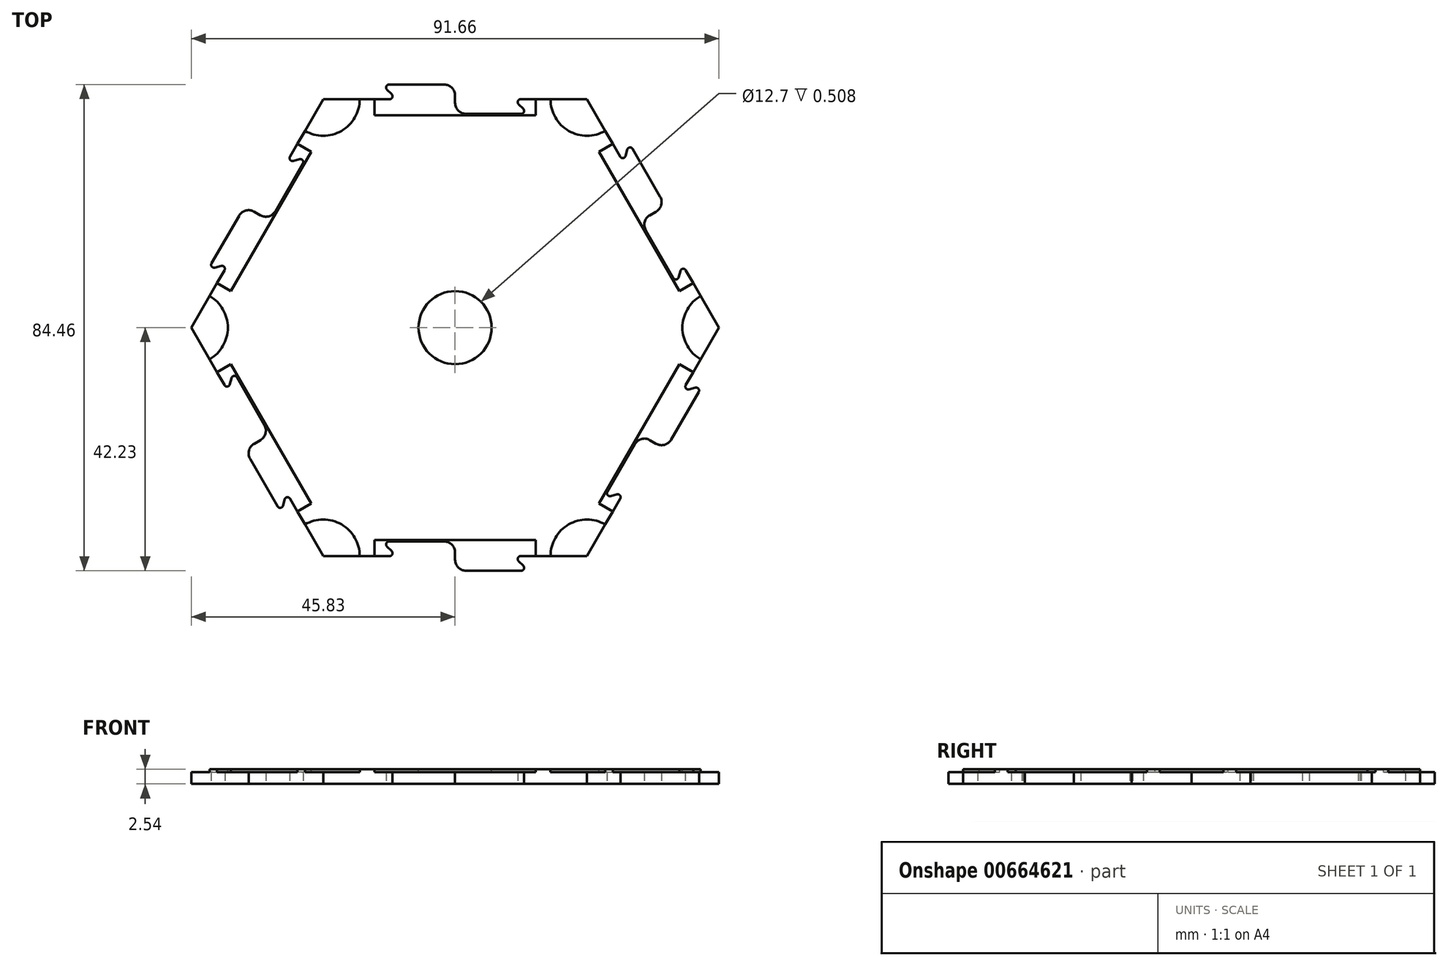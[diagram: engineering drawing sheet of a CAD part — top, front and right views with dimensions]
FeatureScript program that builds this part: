
annotation { "Feature Type Name" : "Feature", "Feature Type Description" : "" }
export const myFeature = defineFeature(function(context is Context, id is Id, definition is map)
    precondition{}
    {
        {
            var Q0;
            Q0=qCreatedBy(makeId("Top.planeOp"),FACE);
            var sketch = newSketch(context, id + "F0", { "sketchPlane" : qUnion([Q0])});
            skCircle(sketch, "E0.cCircle", {"center": v(0, -26.46) * mm, "radius": 13.23 * mm, "construction": true});
            skLineSegment(sketch, "E0.0", {"start": v(22.91, -39.69) * mm, "end": v(-22.91, -39.69) * mm});
            skLineSegment(sketch, "E0.1", {"start": v(-22.91, -39.69) * mm, "end": v(0, 0) * mm});
            skLineSegment(sketch, "E0.2", {"start": v(0, 0) * mm, "end": v(22.91, -39.69) * mm});
            skPoint(sketch, "E0.0.midPoint", {"position": v(0, -39.69) * mm});
            skLineSegment(sketch, "E1", {"start": v(0, -39.69) * mm, "end": v(0, -40.32) * mm});
            skLineSegment(sketch, "E2", {"start": v(1.9, -42.23) * mm, "end": v(11.47, -42.23) * mm});
            skLineSegment(sketch, "E3", {"start": v(11.83, -41.36) * mm, "end": v(11.03, -40.55) * mm});
            skPoint(sketch, "E4.visualSharp", {"position": v(0, -42.23) * mm});
            skPoint(sketch, "E5.visualSharp", {"position": v(12.7, -42.23) * mm});
            skArc(sketch, "E5.filletArc", {"start": v(11.47, -42.23) * mm, "mid": v(11.94, -41.91) * mm, "end": v(11.83, -41.36) * mm});
            skLineSegment(sketch, "E6", {"start": v(11.39, -39.69) * mm, "end": v(22.91, -39.69) * mm});
            skArc(sketch, "E7.filletArc", {"start": v(11.39, -39.69) * mm, "mid": v(10.92, -40) * mm, "end": v(11.03, -40.55) * mm});
            skArc(sketch, "E8.filletArc", {"start": v(0, -40.32) * mm, "mid": v(0.56, -41.67) * mm, "end": v(1.9, -42.23) * mm});
            skLineSegment(sketch, "E9.1.0", {"start": v(-1.9, -37.15) * mm, "end": v(-11.47, -37.15) * mm});
            skArc(sketch, "E9.1.1", {"start": v(0, -39.05) * mm, "mid": v(-0.56, -37.7) * mm, "end": v(-1.9, -37.15) * mm});
            skLineSegment(sketch, "E9.1.2", {"start": v(0, -39.69) * mm, "end": v(0, -39.05) * mm});
            skLineSegment(sketch, "E9.1.3", {"start": v(-11.83, -38.01) * mm, "end": v(-11.03, -38.82) * mm});
            skArc(sketch, "E9.1.4", {"start": v(-11.39, -39.69) * mm, "mid": v(-10.92, -39.37) * mm, "end": v(-11.03, -38.82) * mm});
            skArc(sketch, "E9.1.5", {"start": v(-11.47, -37.15) * mm, "mid": v(-11.94, -37.46) * mm, "end": v(-11.83, -38.01) * mm});
            skSolve(sketch);
        }
        {
            var Q0;
            {var subQ0=sQuery(id+"F0.wireOp",EDGE,"E0.1");Q0=makeQuery(id+"F0.imprint","IMPRINT",FACE,{"disambiguationData":[TD([[makeQuery(id+"F0.imprint","IMPRINT",EDGE,{"derivedFrom":subQ0}),-1.0]])]});}
            var Q1;
            {var subQ0=sQuery(id+"F0.wireOp",EDGE,"97a6bddb-cc4e-44b6-bba3-12cff80ae4aa2.MirrorCS");Q1=makeQuery(id+"F0.imprint","IMPRINT",FACE,{"disambiguationData":[TD([[makeQuery(id+"F0.imprint","IMPRINT",EDGE,{"derivedFrom":subQ0}),-1.0]])]});}
            var Q2;
            {var subQ0=sQuery(id+"F0.wireOp",EDGE,"97a6bddb-cc4e-44b6-bba3-12cff80ae4aa1.MirrorCS");Q2=makeQuery(id+"F0.imprint","IMPRINT",FACE,{"disambiguationData":[TD([[makeQuery(id+"F0.imprint","IMPRINT",EDGE,{"derivedFrom":subQ0}),-1.0]])]});}
            var Q3;
            {var subQ0=sQuery(id+"F0.wireOp",EDGE,"97a6bddb-cc4e-44b6-bba3-12cff80ae4aa0.MirrorCS");Q3=makeQuery(id+"F0.imprint","IMPRINT",FACE,{"disambiguationData":[TD([[makeQuery(id+"F0.imprint","IMPRINT",EDGE,{"derivedFrom":subQ0}),-1.0]])]});}
            var Q4;
            {var subQ0=sQuery(id+"F0.wireOp",EDGE,"bf1687b6-3201-489e-a830-a7b10a865e700.MirrorCS");Q4=makeQuery(id+"F0.imprint","IMPRINT",FACE,{"disambiguationData":[TD([[makeQuery(id+"F0.imprint","IMPRINT",EDGE,{"derivedFrom":subQ0}),-1.0]])]});}
            var Q5;
            {var subQ0=sQuery(id+"F0.wireOp",EDGE,"e4fa4f41-507d-49eb-8017-fd13d7fb7afb0.MirrorCS");Q5=makeQuery(id+"F0.imprint","IMPRINT",FACE,{"disambiguationData":[TD([[makeQuery(id+"F0.imprint","IMPRINT",EDGE,{"derivedFrom":subQ0}),-1.0]])]});}
            var Q6;
            {var subQ0=sQuery(id+"F0.wireOp",EDGE,"ce523281-1682-42e5-b175-8e6fab38ec800.MirrorCS");Q6=makeQuery(id+"F0.imprint","IMPRINT",FACE,{"disambiguationData":[TD([[makeQuery(id+"F0.imprint","IMPRINT",EDGE,{"derivedFrom":subQ0}),-1.0]])]});}
            var Q7;
            {var subQ0=sQuery(id+"F0.wireOp",EDGE,"d5b8cde3-618e-44ad-8592-c6a08a5388a20.MirrorCS");Q7=makeQuery(id+"F0.imprint","IMPRINT",FACE,{"disambiguationData":[TD([[makeQuery(id+"F0.imprint","IMPRINT",EDGE,{"derivedFrom":subQ0}),-1.0]])]});}
            var Q8;
            {var subQ0=sQuery(id+"F0.wireOp",EDGE,"a88186e3-5a36-4d69-b793-0797718b3cf90.MirrorCS");Q8=makeQuery(id+"F0.imprint","IMPRINT",FACE,{"disambiguationData":[TD([[makeQuery(id+"F0.imprint","IMPRINT",EDGE,{"derivedFrom":subQ0}),-1.0]])]});}
            var Q9;
            {var subQ0=sQuery(id+"F0.wireOp",EDGE,"b8ba4a25-16ed-4d6a-869f-626e8081a0210.MirrorCS");Q9=makeQuery(id+"F0.imprint","IMPRINT",FACE,{"disambiguationData":[TD([[makeQuery(id+"F0.imprint","IMPRINT",EDGE,{"derivedFrom":subQ0}),-1.0]])]});}
            var Q10;
            {var subQ0=sQuery(id+"F0.wireOp",EDGE,"5b914c75-573c-406b-9c57-d630d5a647c60.MirrorCS");Q10=makeQuery(id+"F0.imprint","IMPRINT",FACE,{"disambiguationData":[TD([[makeQuery(id+"F0.imprint","IMPRINT",EDGE,{"derivedFrom":subQ0}),-1.0]])]});}
            var Q11;
            {var subQ0=sQuery(id+"F0.wireOp",EDGE,"7752e346-6ae3-4903-9fef-7c2ba14c38f10.MirrorCS");Q11=makeQuery(id+"F0.imprint","IMPRINT",FACE,{"disambiguationData":[TD([[makeQuery(id+"F0.imprint","IMPRINT",EDGE,{"derivedFrom":subQ0}),-1.0]])]});}
            var Q12;
            {var subQ0=sQuery(id+"F0.wireOp",EDGE,"67ecb135-220a-48f5-8a20-4e4477ede5310.MirrorCS");Q12=makeQuery(id+"F0.imprint","IMPRINT",FACE,{"disambiguationData":[TD([[makeQuery(id+"F0.imprint","IMPRINT",EDGE,{"derivedFrom":subQ0}),-1.0]])]});}
            var Q13;
            {var subQ0=sQuery(id+"F0.wireOp",EDGE,"chmzN1dF-lVPi-ufDX-51Gh-vAFPaPJtTRV7");Q13=makeQuery(id+"F0.imprint","IMPRINT",FACE,{"disambiguationData":[TD([[makeQuery(id+"F0.imprint","IMPRINT",EDGE,{"derivedFrom":subQ0}),-1.0]])]});}
            var Q14;
            {var subQ0=sQuery(id+"F0.wireOp",EDGE,"xmj2q76Y-8T0x-Uy3E-bdky-wkXMybDKTkoC");Q14=makeQuery(id+"F0.imprint","IMPRINT",FACE,{"disambiguationData":[TD([[makeQuery(id+"F0.imprint","IMPRINT",EDGE,{"derivedFrom":subQ0}),-1.0]])]});}
            var Q15;
            {var subQ0=sQuery(id+"F0.wireOp",EDGE,"hptf5S9C-4OT9-Tymd-WndI-nW2AmtLXeZ2Y");Q15=makeQuery(id+"F0.imprint","IMPRINT",FACE,{"disambiguationData":[TD([[makeQuery(id+"F0.imprint","IMPRINT",EDGE,{"derivedFrom":subQ0}),-1.0]])]});}
            var Q16;
            {var subQ0=sQuery(id+"F0.wireOp",EDGE,"E1");Q16=makeQuery(id+"F0.imprint","IMPRINT",FACE,{"disambiguationData":[TD([[makeQuery(id+"F0.imprint","IMPRINT",EDGE,{"derivedFrom":subQ0}),1.0]])]});}
            extrude(context, id + "F1", {"entities" : qUnion([Q0, Q1, Q2, Q3, Q4, Q5, Q6, Q7, Q8, Q9, Q10, Q11, Q12, Q13, Q14, Q15, Q16]), "depth" : 2.54 * mm, "offsetDistance" : 25.4 * mm});
        }
        {
            var Q0;
            Q0=makeQuery(id+"F1.opExtrude","SWEPT_BODY",BODY,{"disambiguationData":[OSD([sQuery(id+"F0.wireOp",EDGE,"E0.0"),sQuery(id+"F0.wireOp",EDGE,"E0.1"),sQuery(id+"F0.wireOp",EDGE,"E0.2"),sQuery(id+"F0.wireOp",EDGE,"Ihc1fdpb-C9ge-KW9p-kyAT-bs0RLZlIlIaE"),sQuery(id+"F0.wireOp",EDGE,"87ea3ed5-fdca-4bcd-8325-5824a1b2b9b6.1.0.0"),sQuery(id+"F0.wireOp",EDGE,"87ea3ed5-fdca-4bcd-8325-5824a1b2b9b6.2.0.0"),sQuery(id+"F0.wireOp",EDGE,"87ea3ed5-fdca-4bcd-8325-5824a1b2b9b6.3.0.0"),sQuery(id+"F0.wireOp",EDGE,"be1f27a8-b5cd-4a3d-9b83-b1ceea2719dc.1.0.0"),sQuery(id+"F0.wireOp",EDGE,"be1f27a8-b5cd-4a3d-9b83-b1ceea2719dc.2.0.0"),sQuery(id+"F0.wireOp",EDGE,"be1f27a8-b5cd-4a3d-9b83-b1ceea2719dc.3.0.0"),sQuery(id+"F0.wireOp",EDGE,"be1f27a8-b5cd-4a3d-9b83-b1ceea2719dc.4.0.0"),sQuery(id+"F0.wireOp",EDGE,"97a6bddb-cc4e-44b6-bba3-12cff80ae4aa0.MirrorCS"),sQuery(id+"F0.wireOp",EDGE,"97a6bddb-cc4e-44b6-bba3-12cff80ae4aa1.MirrorCS"),sQuery(id+"F0.wireOp",EDGE,"97a6bddb-cc4e-44b6-bba3-12cff80ae4aa2.MirrorCS"),sQuery(id+"F0.wireOp",EDGE,"bf1687b6-3201-489e-a830-a7b10a865e700.MirrorCS"),sQuery(id+"F0.wireOp",EDGE,"e4fa4f41-507d-49eb-8017-fd13d7fb7afb0.MirrorCS"),sQuery(id+"F0.wireOp",EDGE,"ce523281-1682-42e5-b175-8e6fab38ec800.MirrorCS"),sQuery(id+"F0.wireOp",EDGE,"d5b8cde3-618e-44ad-8592-c6a08a5388a20.MirrorCS"),sQuery(id+"F0.wireOp",EDGE,"a88186e3-5a36-4d69-b793-0797718b3cf90.MirrorCS")])]});
            var Q1;
            Q1=makeQuery(id+"F1.opExtrude","SWEPT_EDGE",EDGE,{"disambiguationData":[OSD([sQuery(id+"F0.wireOp",EDGE,"E0.1"),sQuery(id+"F0.wireOp",EDGE,"E0.2")])]});
            circularPattern(context, id + "F2", {"entities" : qUnion([Q0]), "axis" : qUnion([Q1]), "angle" : 360 * degree, "instanceCount" : 6, "equalSpace" : true});
        }
        {
            var Q0;
            Q0=makeQuery(id+"F1.opExtrude","SWEPT_BODY",BODY,{"disambiguationData":[OSD([sQuery(id+"F0.wireOp",EDGE,"E0.0"),sQuery(id+"F0.wireOp",EDGE,"E0.1"),sQuery(id+"F0.wireOp",EDGE,"E0.2"),sQuery(id+"F0.wireOp",EDGE,"Ihc1fdpb-C9ge-KW9p-kyAT-bs0RLZlIlIaE"),sQuery(id+"F0.wireOp",EDGE,"87ea3ed5-fdca-4bcd-8325-5824a1b2b9b6.1.0.0"),sQuery(id+"F0.wireOp",EDGE,"87ea3ed5-fdca-4bcd-8325-5824a1b2b9b6.2.0.0"),sQuery(id+"F0.wireOp",EDGE,"87ea3ed5-fdca-4bcd-8325-5824a1b2b9b6.3.0.0"),sQuery(id+"F0.wireOp",EDGE,"be1f27a8-b5cd-4a3d-9b83-b1ceea2719dc.1.0.0"),sQuery(id+"F0.wireOp",EDGE,"be1f27a8-b5cd-4a3d-9b83-b1ceea2719dc.2.0.0"),sQuery(id+"F0.wireOp",EDGE,"be1f27a8-b5cd-4a3d-9b83-b1ceea2719dc.3.0.0"),sQuery(id+"F0.wireOp",EDGE,"be1f27a8-b5cd-4a3d-9b83-b1ceea2719dc.4.0.0"),sQuery(id+"F0.wireOp",EDGE,"97a6bddb-cc4e-44b6-bba3-12cff80ae4aa0.MirrorCS"),sQuery(id+"F0.wireOp",EDGE,"97a6bddb-cc4e-44b6-bba3-12cff80ae4aa1.MirrorCS"),sQuery(id+"F0.wireOp",EDGE,"97a6bddb-cc4e-44b6-bba3-12cff80ae4aa2.MirrorCS"),sQuery(id+"F0.wireOp",EDGE,"bf1687b6-3201-489e-a830-a7b10a865e700.MirrorCS"),sQuery(id+"F0.wireOp",EDGE,"e4fa4f41-507d-49eb-8017-fd13d7fb7afb0.MirrorCS"),sQuery(id+"F0.wireOp",EDGE,"ce523281-1682-42e5-b175-8e6fab38ec800.MirrorCS"),sQuery(id+"F0.wireOp",EDGE,"d5b8cde3-618e-44ad-8592-c6a08a5388a20.MirrorCS"),sQuery(id+"F0.wireOp",EDGE,"a88186e3-5a36-4d69-b793-0797718b3cf90.MirrorCS")])]});
            var Q1;
            Q1=makeQuery(id+"F2.opPattern","COPY",BODY,{"derivedFrom":makeQuery(id+"F1.opExtrude","SWEPT_BODY",BODY,{"disambiguationData":[OSD([sQuery(id+"F0.wireOp",EDGE,"E0.0"),sQuery(id+"F0.wireOp",EDGE,"E0.1"),sQuery(id+"F0.wireOp",EDGE,"E0.2"),sQuery(id+"F0.wireOp",EDGE,"Ihc1fdpb-C9ge-KW9p-kyAT-bs0RLZlIlIaE"),sQuery(id+"F0.wireOp",EDGE,"87ea3ed5-fdca-4bcd-8325-5824a1b2b9b6.1.0.0"),sQuery(id+"F0.wireOp",EDGE,"87ea3ed5-fdca-4bcd-8325-5824a1b2b9b6.2.0.0"),sQuery(id+"F0.wireOp",EDGE,"87ea3ed5-fdca-4bcd-8325-5824a1b2b9b6.3.0.0"),sQuery(id+"F0.wireOp",EDGE,"be1f27a8-b5cd-4a3d-9b83-b1ceea2719dc.1.0.0"),sQuery(id+"F0.wireOp",EDGE,"be1f27a8-b5cd-4a3d-9b83-b1ceea2719dc.2.0.0"),sQuery(id+"F0.wireOp",EDGE,"be1f27a8-b5cd-4a3d-9b83-b1ceea2719dc.3.0.0"),sQuery(id+"F0.wireOp",EDGE,"be1f27a8-b5cd-4a3d-9b83-b1ceea2719dc.4.0.0"),sQuery(id+"F0.wireOp",EDGE,"97a6bddb-cc4e-44b6-bba3-12cff80ae4aa0.MirrorCS"),sQuery(id+"F0.wireOp",EDGE,"97a6bddb-cc4e-44b6-bba3-12cff80ae4aa1.MirrorCS"),sQuery(id+"F0.wireOp",EDGE,"97a6bddb-cc4e-44b6-bba3-12cff80ae4aa2.MirrorCS"),sQuery(id+"F0.wireOp",EDGE,"bf1687b6-3201-489e-a830-a7b10a865e700.MirrorCS"),sQuery(id+"F0.wireOp",EDGE,"e4fa4f41-507d-49eb-8017-fd13d7fb7afb0.MirrorCS"),sQuery(id+"F0.wireOp",EDGE,"ce523281-1682-42e5-b175-8e6fab38ec800.MirrorCS"),sQuery(id+"F0.wireOp",EDGE,"d5b8cde3-618e-44ad-8592-c6a08a5388a20.MirrorCS"),sQuery(id+"F0.wireOp",EDGE,"a88186e3-5a36-4d69-b793-0797718b3cf90.MirrorCS")])]}),"instanceName":"1"});
            var Q2;
            Q2=makeQuery(id+"F2.opPattern","COPY",BODY,{"derivedFrom":makeQuery(id+"F1.opExtrude","SWEPT_BODY",BODY,{"disambiguationData":[OSD([sQuery(id+"F0.wireOp",EDGE,"E0.0"),sQuery(id+"F0.wireOp",EDGE,"E0.1"),sQuery(id+"F0.wireOp",EDGE,"E0.2"),sQuery(id+"F0.wireOp",EDGE,"Ihc1fdpb-C9ge-KW9p-kyAT-bs0RLZlIlIaE"),sQuery(id+"F0.wireOp",EDGE,"87ea3ed5-fdca-4bcd-8325-5824a1b2b9b6.1.0.0"),sQuery(id+"F0.wireOp",EDGE,"87ea3ed5-fdca-4bcd-8325-5824a1b2b9b6.2.0.0"),sQuery(id+"F0.wireOp",EDGE,"87ea3ed5-fdca-4bcd-8325-5824a1b2b9b6.3.0.0"),sQuery(id+"F0.wireOp",EDGE,"be1f27a8-b5cd-4a3d-9b83-b1ceea2719dc.1.0.0"),sQuery(id+"F0.wireOp",EDGE,"be1f27a8-b5cd-4a3d-9b83-b1ceea2719dc.2.0.0"),sQuery(id+"F0.wireOp",EDGE,"be1f27a8-b5cd-4a3d-9b83-b1ceea2719dc.3.0.0"),sQuery(id+"F0.wireOp",EDGE,"be1f27a8-b5cd-4a3d-9b83-b1ceea2719dc.4.0.0"),sQuery(id+"F0.wireOp",EDGE,"97a6bddb-cc4e-44b6-bba3-12cff80ae4aa0.MirrorCS"),sQuery(id+"F0.wireOp",EDGE,"97a6bddb-cc4e-44b6-bba3-12cff80ae4aa1.MirrorCS"),sQuery(id+"F0.wireOp",EDGE,"97a6bddb-cc4e-44b6-bba3-12cff80ae4aa2.MirrorCS"),sQuery(id+"F0.wireOp",EDGE,"bf1687b6-3201-489e-a830-a7b10a865e700.MirrorCS"),sQuery(id+"F0.wireOp",EDGE,"e4fa4f41-507d-49eb-8017-fd13d7fb7afb0.MirrorCS"),sQuery(id+"F0.wireOp",EDGE,"ce523281-1682-42e5-b175-8e6fab38ec800.MirrorCS"),sQuery(id+"F0.wireOp",EDGE,"d5b8cde3-618e-44ad-8592-c6a08a5388a20.MirrorCS"),sQuery(id+"F0.wireOp",EDGE,"a88186e3-5a36-4d69-b793-0797718b3cf90.MirrorCS")])]}),"instanceName":"2"});
            var Q3;
            Q3=makeQuery(id+"F2.opPattern","COPY",BODY,{"derivedFrom":makeQuery(id+"F1.opExtrude","SWEPT_BODY",BODY,{"disambiguationData":[OSD([sQuery(id+"F0.wireOp",EDGE,"E0.0"),sQuery(id+"F0.wireOp",EDGE,"E0.1"),sQuery(id+"F0.wireOp",EDGE,"E0.2"),sQuery(id+"F0.wireOp",EDGE,"Ihc1fdpb-C9ge-KW9p-kyAT-bs0RLZlIlIaE"),sQuery(id+"F0.wireOp",EDGE,"87ea3ed5-fdca-4bcd-8325-5824a1b2b9b6.1.0.0"),sQuery(id+"F0.wireOp",EDGE,"87ea3ed5-fdca-4bcd-8325-5824a1b2b9b6.2.0.0"),sQuery(id+"F0.wireOp",EDGE,"87ea3ed5-fdca-4bcd-8325-5824a1b2b9b6.3.0.0"),sQuery(id+"F0.wireOp",EDGE,"be1f27a8-b5cd-4a3d-9b83-b1ceea2719dc.1.0.0"),sQuery(id+"F0.wireOp",EDGE,"be1f27a8-b5cd-4a3d-9b83-b1ceea2719dc.2.0.0"),sQuery(id+"F0.wireOp",EDGE,"be1f27a8-b5cd-4a3d-9b83-b1ceea2719dc.3.0.0"),sQuery(id+"F0.wireOp",EDGE,"be1f27a8-b5cd-4a3d-9b83-b1ceea2719dc.4.0.0"),sQuery(id+"F0.wireOp",EDGE,"97a6bddb-cc4e-44b6-bba3-12cff80ae4aa0.MirrorCS"),sQuery(id+"F0.wireOp",EDGE,"97a6bddb-cc4e-44b6-bba3-12cff80ae4aa1.MirrorCS"),sQuery(id+"F0.wireOp",EDGE,"97a6bddb-cc4e-44b6-bba3-12cff80ae4aa2.MirrorCS"),sQuery(id+"F0.wireOp",EDGE,"bf1687b6-3201-489e-a830-a7b10a865e700.MirrorCS"),sQuery(id+"F0.wireOp",EDGE,"e4fa4f41-507d-49eb-8017-fd13d7fb7afb0.MirrorCS"),sQuery(id+"F0.wireOp",EDGE,"ce523281-1682-42e5-b175-8e6fab38ec800.MirrorCS"),sQuery(id+"F0.wireOp",EDGE,"d5b8cde3-618e-44ad-8592-c6a08a5388a20.MirrorCS"),sQuery(id+"F0.wireOp",EDGE,"a88186e3-5a36-4d69-b793-0797718b3cf90.MirrorCS")])]}),"instanceName":"3"});
            var Q4;
            Q4=makeQuery(id+"F2.opPattern","COPY",BODY,{"derivedFrom":makeQuery(id+"F1.opExtrude","SWEPT_BODY",BODY,{"disambiguationData":[OSD([sQuery(id+"F0.wireOp",EDGE,"E0.0"),sQuery(id+"F0.wireOp",EDGE,"E0.1"),sQuery(id+"F0.wireOp",EDGE,"E0.2"),sQuery(id+"F0.wireOp",EDGE,"Ihc1fdpb-C9ge-KW9p-kyAT-bs0RLZlIlIaE"),sQuery(id+"F0.wireOp",EDGE,"87ea3ed5-fdca-4bcd-8325-5824a1b2b9b6.1.0.0"),sQuery(id+"F0.wireOp",EDGE,"87ea3ed5-fdca-4bcd-8325-5824a1b2b9b6.2.0.0"),sQuery(id+"F0.wireOp",EDGE,"87ea3ed5-fdca-4bcd-8325-5824a1b2b9b6.3.0.0"),sQuery(id+"F0.wireOp",EDGE,"be1f27a8-b5cd-4a3d-9b83-b1ceea2719dc.1.0.0"),sQuery(id+"F0.wireOp",EDGE,"be1f27a8-b5cd-4a3d-9b83-b1ceea2719dc.2.0.0"),sQuery(id+"F0.wireOp",EDGE,"be1f27a8-b5cd-4a3d-9b83-b1ceea2719dc.3.0.0"),sQuery(id+"F0.wireOp",EDGE,"be1f27a8-b5cd-4a3d-9b83-b1ceea2719dc.4.0.0"),sQuery(id+"F0.wireOp",EDGE,"97a6bddb-cc4e-44b6-bba3-12cff80ae4aa0.MirrorCS"),sQuery(id+"F0.wireOp",EDGE,"97a6bddb-cc4e-44b6-bba3-12cff80ae4aa1.MirrorCS"),sQuery(id+"F0.wireOp",EDGE,"97a6bddb-cc4e-44b6-bba3-12cff80ae4aa2.MirrorCS"),sQuery(id+"F0.wireOp",EDGE,"bf1687b6-3201-489e-a830-a7b10a865e700.MirrorCS"),sQuery(id+"F0.wireOp",EDGE,"e4fa4f41-507d-49eb-8017-fd13d7fb7afb0.MirrorCS"),sQuery(id+"F0.wireOp",EDGE,"ce523281-1682-42e5-b175-8e6fab38ec800.MirrorCS"),sQuery(id+"F0.wireOp",EDGE,"d5b8cde3-618e-44ad-8592-c6a08a5388a20.MirrorCS"),sQuery(id+"F0.wireOp",EDGE,"a88186e3-5a36-4d69-b793-0797718b3cf90.MirrorCS")])]}),"instanceName":"4"});
            var Q5;
            Q5=makeQuery(id+"F2.opPattern","COPY",BODY,{"derivedFrom":makeQuery(id+"F1.opExtrude","SWEPT_BODY",BODY,{"disambiguationData":[OSD([sQuery(id+"F0.wireOp",EDGE,"E0.0"),sQuery(id+"F0.wireOp",EDGE,"E0.1"),sQuery(id+"F0.wireOp",EDGE,"E0.2"),sQuery(id+"F0.wireOp",EDGE,"Ihc1fdpb-C9ge-KW9p-kyAT-bs0RLZlIlIaE"),sQuery(id+"F0.wireOp",EDGE,"87ea3ed5-fdca-4bcd-8325-5824a1b2b9b6.1.0.0"),sQuery(id+"F0.wireOp",EDGE,"87ea3ed5-fdca-4bcd-8325-5824a1b2b9b6.2.0.0"),sQuery(id+"F0.wireOp",EDGE,"87ea3ed5-fdca-4bcd-8325-5824a1b2b9b6.3.0.0"),sQuery(id+"F0.wireOp",EDGE,"be1f27a8-b5cd-4a3d-9b83-b1ceea2719dc.1.0.0"),sQuery(id+"F0.wireOp",EDGE,"be1f27a8-b5cd-4a3d-9b83-b1ceea2719dc.2.0.0"),sQuery(id+"F0.wireOp",EDGE,"be1f27a8-b5cd-4a3d-9b83-b1ceea2719dc.3.0.0"),sQuery(id+"F0.wireOp",EDGE,"be1f27a8-b5cd-4a3d-9b83-b1ceea2719dc.4.0.0"),sQuery(id+"F0.wireOp",EDGE,"97a6bddb-cc4e-44b6-bba3-12cff80ae4aa0.MirrorCS"),sQuery(id+"F0.wireOp",EDGE,"97a6bddb-cc4e-44b6-bba3-12cff80ae4aa1.MirrorCS"),sQuery(id+"F0.wireOp",EDGE,"97a6bddb-cc4e-44b6-bba3-12cff80ae4aa2.MirrorCS"),sQuery(id+"F0.wireOp",EDGE,"bf1687b6-3201-489e-a830-a7b10a865e700.MirrorCS"),sQuery(id+"F0.wireOp",EDGE,"e4fa4f41-507d-49eb-8017-fd13d7fb7afb0.MirrorCS"),sQuery(id+"F0.wireOp",EDGE,"ce523281-1682-42e5-b175-8e6fab38ec800.MirrorCS"),sQuery(id+"F0.wireOp",EDGE,"d5b8cde3-618e-44ad-8592-c6a08a5388a20.MirrorCS"),sQuery(id+"F0.wireOp",EDGE,"a88186e3-5a36-4d69-b793-0797718b3cf90.MirrorCS")])]}),"instanceName":"5"});
            booleanBodies(context, id + "F3", {"operationType" : BooleanOperationType.UNION, "tools" : qUnion([Q0, Q1, Q2, Q3, Q4, Q5])});
        }
        {
            var Q0;
            {var subQ0=makeQuery(id+"F1.opExtrude","CAP_FACE",FACE,{"disambiguationData":[OSD([sQuery(id+"F0.wireOp",EDGE,"E0.0"),sQuery(id+"F0.wireOp",EDGE,"E0.1"),sQuery(id+"F0.wireOp",EDGE,"E0.2"),sQuery(id+"F0.wireOp",EDGE,"E1"),sQuery(id+"F0.wireOp",EDGE,"E2"),sQuery(id+"F0.wireOp",EDGE,"E3"),sQuery(id+"F0.wireOp",EDGE,"E5.filletArc"),sQuery(id+"F0.wireOp",EDGE,"E6"),sQuery(id+"F0.wireOp",EDGE,"E7.filletArc"),sQuery(id+"F0.wireOp",EDGE,"E8.filletArc"),sQuery(id+"F0.wireOp",EDGE,"E9.1.0"),sQuery(id+"F0.wireOp",EDGE,"E9.1.1"),sQuery(id+"F0.wireOp",EDGE,"E9.1.2"),sQuery(id+"F0.wireOp",EDGE,"E9.1.3"),sQuery(id+"F0.wireOp",EDGE,"E9.1.4"),sQuery(id+"F0.wireOp",EDGE,"E9.1.5")])],"isStart":false});Q0=makeQuery(id+"F3.opBoolean","MERGE",FACE,{"derivedFrom":[subQ0,makeQuery(id+"F2.opPattern","COPY",FACE,{"derivedFrom":subQ0,"instanceName":"1"}),makeQuery(id+"F2.opPattern","COPY",FACE,{"derivedFrom":subQ0,"instanceName":"2"}),makeQuery(id+"F2.opPattern","COPY",FACE,{"derivedFrom":subQ0,"instanceName":"3"}),makeQuery(id+"F2.opPattern","COPY",FACE,{"derivedFrom":subQ0,"instanceName":"4"}),makeQuery(id+"F2.opPattern","COPY",FACE,{"derivedFrom":subQ0,"instanceName":"5"})]});}
            var sketch = newSketch(context, id + "F4", { "sketchPlane" : qUnion([Q0])});
            skLineSegment(sketch, "E10.bottom", {"start": v(-13.97, -36.9) * mm, "end": v(13.97, -36.9) * mm});
            skLineSegment(sketch, "E10.top", {"start": v(-13.97, -42.48) * mm, "end": v(13.97, -42.48) * mm});
            skLineSegment(sketch, "E10.left", {"start": v(-13.97, -36.9) * mm, "end": v(-13.97, -42.48) * mm});
            skLineSegment(sketch, "E10.right", {"start": v(13.97, -36.9) * mm, "end": v(13.97, -42.48) * mm});
            skCircle(sketch, "E11", {"center": v(0, 0) * mm, "radius": 6.35 * mm});
            skLineSegment(sketch, "E12.1.0", {"start": v(29.8, -33.34) * mm, "end": v(43.78, -9.14) * mm});
            skLineSegment(sketch, "E12.1.1", {"start": v(24.97, -30.55) * mm, "end": v(29.8, -33.34) * mm});
            skLineSegment(sketch, "E12.1.2", {"start": v(24.97, -30.55) * mm, "end": v(38.94, -6.35) * mm});
            skLineSegment(sketch, "E12.1.3", {"start": v(38.94, -6.35) * mm, "end": v(43.78, -9.14) * mm});
            skLineSegment(sketch, "E12.2.0", {"start": v(43.78, 9.14) * mm, "end": v(29.8, 33.34) * mm});
            skLineSegment(sketch, "E12.2.1", {"start": v(38.94, 6.35) * mm, "end": v(43.78, 9.14) * mm});
            skLineSegment(sketch, "E12.2.2", {"start": v(38.94, 6.35) * mm, "end": v(24.97, 30.55) * mm});
            skLineSegment(sketch, "E12.2.3", {"start": v(24.97, 30.55) * mm, "end": v(29.8, 33.34) * mm});
            skLineSegment(sketch, "E12.3.0", {"start": v(13.97, 42.48) * mm, "end": v(-13.97, 42.48) * mm});
            skLineSegment(sketch, "E12.3.1", {"start": v(13.97, 36.9) * mm, "end": v(13.97, 42.48) * mm});
            skLineSegment(sketch, "E12.3.2", {"start": v(13.97, 36.9) * mm, "end": v(-13.97, 36.9) * mm});
            skLineSegment(sketch, "E12.3.3", {"start": v(-13.97, 36.9) * mm, "end": v(-13.97, 42.48) * mm});
            skLineSegment(sketch, "E12.4.0", {"start": v(-29.8, 33.34) * mm, "end": v(-43.78, 9.14) * mm});
            skLineSegment(sketch, "E12.4.1", {"start": v(-24.97, 30.55) * mm, "end": v(-29.8, 33.34) * mm});
            skLineSegment(sketch, "E12.4.2", {"start": v(-24.97, 30.55) * mm, "end": v(-38.94, 6.35) * mm});
            skLineSegment(sketch, "E12.4.3", {"start": v(-38.94, 6.35) * mm, "end": v(-43.78, 9.14) * mm});
            skLineSegment(sketch, "E12.5.0", {"start": v(-43.78, -9.14) * mm, "end": v(-29.8, -33.34) * mm});
            skLineSegment(sketch, "E12.5.1", {"start": v(-38.94, -6.35) * mm, "end": v(-43.78, -9.14) * mm});
            skLineSegment(sketch, "E12.5.2", {"start": v(-38.94, -6.35) * mm, "end": v(-24.97, -30.55) * mm});
            skLineSegment(sketch, "E12.5.3", {"start": v(-24.97, -30.55) * mm, "end": v(-29.8, -33.34) * mm});
            skCircle(sketch, "E13", {"center": v(22.91, -39.69) * mm, "radius": 6.35 * mm});
            skCircle(sketch, "E14.1.0", {"center": v(45.83, 0) * mm, "radius": 6.35 * mm});
            skCircle(sketch, "E14.2.0", {"center": v(22.91, 39.69) * mm, "radius": 6.35 * mm});
            skCircle(sketch, "E14.3.0", {"center": v(-22.91, 39.69) * mm, "radius": 6.35 * mm});
            skCircle(sketch, "E14.4.0", {"center": v(-45.83, 0) * mm, "radius": 6.35 * mm});
            skCircle(sketch, "E14.5.0", {"center": v(-22.91, -39.69) * mm, "radius": 6.35 * mm});
            skSolve(sketch);
        }
        {
            var Q0;
            Q0=makeQuery(id+"F4.imprint","IMPRINT",FACE,{"disambiguationData":[TD([[makeQuery(id+"F4.imprint","IMPRINT",EDGE,{"derivedFrom":sQuery(id+"F4.wireOp",EDGE,"E11")}),1.0]])]});
            var Q1;
            Q1=makeQuery(id+"F4.imprint","IMPRINT",FACE,{"disambiguationData":[TD([[makeQuery(id+"F4.imprint","IMPRINT",EDGE,{"derivedFrom":makeQuery(id+"F1.opExtrude","CAP_EDGE",EDGE,{"disambiguationData":[OSD([sQuery(id+"F0.wireOp",EDGE,"E3")])],"isStart":false})}),1.0]])]});
            var Q2;
            Q2=makeQuery(id+"F4.imprint","IMPRINT",FACE,{"disambiguationData":[TD([[makeQuery(id+"F4.imprint","IMPRINT",EDGE,{"derivedFrom":makeQuery(id+"F1.opExtrude","CAP_EDGE",EDGE,{"disambiguationData":[OSD([sQuery(id+"F0.wireOp",EDGE,"E9.1.3")])],"isStart":false})}),-1.0]])]});
            var Q3;
            Q3=makeQuery(id+"F4.imprint","IMPRINT",FACE,{"disambiguationData":[TD([[makeQuery(id+"F4.imprint","IMPRINT",EDGE,{"derivedFrom":makeQuery(id+"F2.opPattern","COPY",EDGE,{"derivedFrom":makeQuery(id+"F1.opExtrude","CAP_EDGE",EDGE,{"disambiguationData":[OSD([sQuery(id+"F0.wireOp",EDGE,"E9.1.3")])],"isStart":false}),"instanceName":"5"})}),-1.0]])]});
            var Q4;
            Q4=makeQuery(id+"F4.imprint","IMPRINT",FACE,{"disambiguationData":[TD([[makeQuery(id+"F4.imprint","IMPRINT",EDGE,{"derivedFrom":makeQuery(id+"F2.opPattern","COPY",EDGE,{"derivedFrom":makeQuery(id+"F1.opExtrude","CAP_EDGE",EDGE,{"disambiguationData":[OSD([sQuery(id+"F0.wireOp",EDGE,"E3")])],"isStart":false}),"instanceName":"5"})}),1.0]])]});
            var Q5;
            Q5=makeQuery(id+"F4.imprint","IMPRINT",FACE,{"disambiguationData":[TD([[makeQuery(id+"F4.imprint","IMPRINT",EDGE,{"derivedFrom":makeQuery(id+"F2.opPattern","COPY",EDGE,{"derivedFrom":makeQuery(id+"F1.opExtrude","CAP_EDGE",EDGE,{"disambiguationData":[OSD([sQuery(id+"F0.wireOp",EDGE,"E9.1.3")])],"isStart":false}),"instanceName":"4"})}),-1.0]])]});
            var Q6;
            Q6=makeQuery(id+"F4.imprint","IMPRINT",FACE,{"disambiguationData":[TD([[makeQuery(id+"F4.imprint","IMPRINT",EDGE,{"derivedFrom":makeQuery(id+"F2.opPattern","COPY",EDGE,{"derivedFrom":makeQuery(id+"F1.opExtrude","CAP_EDGE",EDGE,{"disambiguationData":[OSD([sQuery(id+"F0.wireOp",EDGE,"E3")])],"isStart":false}),"instanceName":"4"})}),1.0]])]});
            var Q7;
            Q7=makeQuery(id+"F4.imprint","IMPRINT",FACE,{"disambiguationData":[TD([[makeQuery(id+"F4.imprint","IMPRINT",EDGE,{"derivedFrom":makeQuery(id+"F2.opPattern","COPY",EDGE,{"derivedFrom":makeQuery(id+"F1.opExtrude","CAP_EDGE",EDGE,{"disambiguationData":[OSD([sQuery(id+"F0.wireOp",EDGE,"E9.1.3")])],"isStart":false}),"instanceName":"3"})}),-1.0]])]});
            var Q8;
            Q8=makeQuery(id+"F4.imprint","IMPRINT",FACE,{"disambiguationData":[TD([[makeQuery(id+"F4.imprint","IMPRINT",EDGE,{"derivedFrom":makeQuery(id+"F2.opPattern","COPY",EDGE,{"derivedFrom":makeQuery(id+"F1.opExtrude","CAP_EDGE",EDGE,{"disambiguationData":[OSD([sQuery(id+"F0.wireOp",EDGE,"E3")])],"isStart":false}),"instanceName":"3"})}),1.0]])]});
            var Q9;
            Q9=makeQuery(id+"F4.imprint","IMPRINT",FACE,{"disambiguationData":[TD([[makeQuery(id+"F4.imprint","IMPRINT",EDGE,{"derivedFrom":makeQuery(id+"F2.opPattern","COPY",EDGE,{"derivedFrom":makeQuery(id+"F1.opExtrude","CAP_EDGE",EDGE,{"disambiguationData":[OSD([sQuery(id+"F0.wireOp",EDGE,"E9.1.3")])],"isStart":false}),"instanceName":"2"})}),-1.0]])]});
            var Q10;
            Q10=makeQuery(id+"F4.imprint","IMPRINT",FACE,{"disambiguationData":[TD([[makeQuery(id+"F4.imprint","IMPRINT",EDGE,{"derivedFrom":makeQuery(id+"F2.opPattern","COPY",EDGE,{"derivedFrom":makeQuery(id+"F1.opExtrude","CAP_EDGE",EDGE,{"disambiguationData":[OSD([sQuery(id+"F0.wireOp",EDGE,"E3")])],"isStart":false}),"instanceName":"2"})}),1.0]])]});
            var Q11;
            Q11=makeQuery(id+"F4.imprint","IMPRINT",FACE,{"disambiguationData":[TD([[makeQuery(id+"F4.imprint","IMPRINT",EDGE,{"derivedFrom":makeQuery(id+"F2.opPattern","COPY",EDGE,{"derivedFrom":makeQuery(id+"F1.opExtrude","CAP_EDGE",EDGE,{"disambiguationData":[OSD([sQuery(id+"F0.wireOp",EDGE,"E9.1.3")])],"isStart":false}),"instanceName":"1"})}),-1.0]])]});
            var Q12;
            Q12=makeQuery(id+"F4.imprint","IMPRINT",FACE,{"disambiguationData":[TD([[makeQuery(id+"F4.imprint","IMPRINT",EDGE,{"derivedFrom":makeQuery(id+"F2.opPattern","COPY",EDGE,{"derivedFrom":makeQuery(id+"F1.opExtrude","CAP_EDGE",EDGE,{"disambiguationData":[OSD([sQuery(id+"F0.wireOp",EDGE,"E3")])],"isStart":false}),"instanceName":"1"})}),1.0]])]});
            var Q13;
            {var subQ0=sQuery(id+"F4.wireOp",EDGE,"E14.5.0");var subQ1=makeQuery(id+"F1.opExtrude","CAP_EDGE",EDGE,{"disambiguationData":[OSD([sQuery(id+"F0.wireOp",EDGE,"E0.0")])],"isStart":false});var subQ2=makeQuery(id+"F4.imprint","INTERSECT",VERTEX,{"derivedFrom":[subQ1,subQ0]});Q13=makeQuery(id+"F4.imprint","IMPRINT",FACE,{"disambiguationData":[TD([[makeQuery(id+"F4.imprint","IMPRINT",EDGE,{"disambiguationData":[TD([[subQ2,-1.0]])],"derivedFrom":subQ0}),1.0]])]});}
            var Q14;
            {var subQ0=sQuery(id+"F4.wireOp",EDGE,"E13");var subQ1=makeQuery(id+"F1.opExtrude","CAP_EDGE",EDGE,{"disambiguationData":[OSD([sQuery(id+"F0.wireOp",EDGE,"E6")])],"isStart":false});var subQ2=makeQuery(id+"F4.imprint","INTERSECT",VERTEX,{"derivedFrom":[subQ1,subQ0]});Q14=makeQuery(id+"F4.imprint","IMPRINT",FACE,{"disambiguationData":[TD([[makeQuery(id+"F4.imprint","IMPRINT",EDGE,{"disambiguationData":[TD([[subQ2,1.0]])],"derivedFrom":subQ0}),1.0]])]});}
            var Q15;
            {var subQ0=sQuery(id+"F4.wireOp",EDGE,"E14.1.0");var subQ1=makeQuery(id+"F2.opPattern","COPY",EDGE,{"derivedFrom":makeQuery(id+"F1.opExtrude","CAP_EDGE",EDGE,{"disambiguationData":[OSD([sQuery(id+"F0.wireOp",EDGE,"E0.0")])],"isStart":false}),"instanceName":"4"});var subQ2=makeQuery(id+"F4.imprint","INTERSECT",VERTEX,{"derivedFrom":[subQ1,subQ0]});Q15=makeQuery(id+"F4.imprint","IMPRINT",FACE,{"disambiguationData":[TD([[makeQuery(id+"F4.imprint","IMPRINT",EDGE,{"disambiguationData":[TD([[subQ2,-1.0]])],"derivedFrom":subQ0}),1.0]])]});}
            var Q16;
            {var subQ0=sQuery(id+"F4.wireOp",EDGE,"E14.2.0");var subQ1=makeQuery(id+"F2.opPattern","COPY",EDGE,{"derivedFrom":makeQuery(id+"F1.opExtrude","CAP_EDGE",EDGE,{"disambiguationData":[OSD([sQuery(id+"F0.wireOp",EDGE,"E0.0")])],"isStart":false}),"instanceName":"3"});var subQ2=makeQuery(id+"F4.imprint","INTERSECT",VERTEX,{"derivedFrom":[subQ1,subQ0]});Q16=makeQuery(id+"F4.imprint","IMPRINT",FACE,{"disambiguationData":[TD([[makeQuery(id+"F4.imprint","IMPRINT",EDGE,{"disambiguationData":[TD([[subQ2,-1.0]])],"derivedFrom":subQ0}),1.0]])]});}
            var Q17;
            {var subQ0=sQuery(id+"F4.wireOp",EDGE,"E14.3.0");var subQ1=makeQuery(id+"F2.opPattern","COPY",EDGE,{"derivedFrom":makeQuery(id+"F1.opExtrude","CAP_EDGE",EDGE,{"disambiguationData":[OSD([sQuery(id+"F0.wireOp",EDGE,"E0.0")])],"isStart":false}),"instanceName":"2"});var subQ2=makeQuery(id+"F4.imprint","INTERSECT",VERTEX,{"derivedFrom":[subQ1,subQ0]});Q17=makeQuery(id+"F4.imprint","IMPRINT",FACE,{"disambiguationData":[TD([[makeQuery(id+"F4.imprint","IMPRINT",EDGE,{"disambiguationData":[TD([[subQ2,-1.0]])],"derivedFrom":subQ0}),1.0]])]});}
            var Q18;
            {var subQ0=sQuery(id+"F4.wireOp",EDGE,"E14.4.0");var subQ1=makeQuery(id+"F2.opPattern","COPY",EDGE,{"derivedFrom":makeQuery(id+"F1.opExtrude","CAP_EDGE",EDGE,{"disambiguationData":[OSD([sQuery(id+"F0.wireOp",EDGE,"E0.0")])],"isStart":false}),"instanceName":"1"});var subQ2=makeQuery(id+"F4.imprint","INTERSECT",VERTEX,{"derivedFrom":[subQ1,subQ0]});Q18=makeQuery(id+"F4.imprint","IMPRINT",FACE,{"disambiguationData":[TD([[makeQuery(id+"F4.imprint","IMPRINT",EDGE,{"disambiguationData":[TD([[subQ2,-1.0]])],"derivedFrom":subQ0}),1.0]])]});}
            extrude(context, id + "F5", {"entities" : qUnion([Q0, Q1, Q2, Q3, Q4, Q5, Q6, Q7, Q8, Q9, Q10, Q11, Q12, Q13, Q14, Q15, Q16, Q17, Q18]), "operationType" : NewBodyOperationType.REMOVE, "oppositeDirection" : true, "depth" : 0.5 * mm, "offsetDistance" : 25.4 * mm});
        }
    });
